# Revit family: equip-water-cooler-elkay-erfp
name_source: partatom
category: Plumbing Fixtures
units: mm (PartAtom-declared; Revit-internal decimal feet)

## family parameters
Always vertical = Yes
Cut with Voids When Loaded = No
OmniClass Number = 23.45.00.00
OmniClass Title = Sanitary, Laundry, and Cleaning Equipment
Part Type = Normal
Room Calculation Point = No
Round Connector Dimension = Use Radius
Shared = No
Work Plane-Based = No

## types (19) — shared parameters
Basin Material = Metal - Steel - Stainless - Chrome
Button Material = Metal - Steel - Stainless - Chrome
CW Connection = Yes
Chiller = ECH8
Cooler Depth = 1' - 6 5/8"
Cooler Separation = 0' - 6 5/8"
Cooler Width = 1' - 0 1/8"
Description = Water Cooler
Dispenser Height = 2' - 9"
HW Connection = No
Lower Cooler Rim Height = 2' - 9 1/2"
Lower Orifice Height = 2' - 11 1/8"
Manufacturer = Elkay
Orifice to Rim = 0' - 1 5/8"
Panel Material = Metal - Steel - Stainless - Chrome
Rim to Dispenser = 0' - 6 1/2"
URL = http://www.elkay.com
Upper Cooler Depth = 1' - 0 7/8"
Upper Cooler Rim Height = 3' - 3 1/2"
Upper Orifice Height = 3' - 5 1/8"
Upper Rim Height = 3' - 3 1/2"
Vent Connection = No
Version = 1.0.0.0
Volts/Hertz = 115V/60Hz
Wall Plate Material = Metal - Steel - Stainless - Chrome
Waste Connection = Yes
Water Service Flow = 0 GPM
Water Service Size Radius = 0' - 0 1/4"

## per-type parameters (varying)
| type | Activation | Bubbler | Filter | Fountain | Glass Filter | Mounting | Type |
| ECRSPM8K | Pushbutton | Flexi-Guard | See LCRSPM8K | ECRSPD8C | - | MFC100 | Single (Child ADA) |
| ECRSP8K | Pushbutton | Flexi-Guard | See LCRSP8K | ECRSPD8C | - | ***Order MFC100 Separately | Single (Child ADA) |
| ECRSPVRM8 | Pushbutton | VR Bubbler | See LNFEM8VRK | ECRSPVRD8C | - | MFC100 | Single (Child ADA) |
| ECRSPVR8K | Pushbutton | VR Bubbler | **ACC (EWF172) | ECRSPVRD8C | - | ***Order MFC100 Separately | Single (Child ADA) |
| ERFPM8K | Pushbutton | Flexi-Guard | See LNFEM8K | ERFPD8FC | See ERFPM8FK | MFC100 | Single |
| ERFP8K | Pushbutton | Flexi-Guard | See LNFE8K | ERFPD8FC | See ERFP8FK | ***Order MF100 Separately | Single |
| ERFPM8FK | Pushbutton | Flexi-Guard | See LNFEM8FK | ERFPD8FC | Factory Prepped (Order GF Separately) | MFC100 | Single |
| ERFP8FK | Pushbutton | Flexi-Guard | See LNFEM8FK | ERFPD8FC | Factory Prepped (Order GF Separately) | ***Order MF100 Separately | Single |
| ERFPVRM8K | Pushbutton | VR Bubbler | **ACC (EWF172) | ERFPVRD8C | - | MFC100 | Single |
| ERFPVR8K | Pushbutton | VR Bubbler | **ACC (EWF172) | ERFPVRD8C | - | ***Order MF100 Separately | Single |
| EROM8K | Sensor | Flexi-Guard | **ACC (EWF172) | EROD8C |  | MFC100 | Single |
| ERO8K | Sensor | Flexi-Guard | **ACC (EWF172) | EROD8C |  | ***Order MF100 Separately | Single |
| LCRSPM8K | Pushbutton | Flexi-Guard | EWF172 | LCRSPD8C | - | MFC100 | Single (Child ADA) |
| LCRSP8K | Pushbutton | Flexi-Guard | EWF172 | LCRSPD8C | - | ***Order MF100 Separately | Single (Child ADA) |
| LNFEM8K | Pushbutton | Flexi-Guard | EWF172 | LNFED8C | See LNTEM8FK | MF100 | Single |
| LNFE8K | Pushbutton | Flexi-Guard | EWF172 | LNFED8C | See LNTE8FK | ***Order MF100 Separately | Single |
| LNFEM8FK | Pushbutton | Flexi-Guard | EWF172 | LNFED8FC | Factory Prepped (Order GF Separately) | MF100 | Single |
| LNFE8FK | Pushbutton | Flexi-Guard | EWF172 | LNFED8FC | Factory Prepped (Order GF Separately) | ***Order MF100 Separately | Single |
| LNFEM8VRK | Pushbutton | VR Bubbler | EWF172 | LNFED8VRC | - | MF100 | Single |

note: column(s) folded — value = type name in every type: Model

## geometry (parser evidence)
native form markers: Sweep x6
no freeform markers — native parametric forms only
